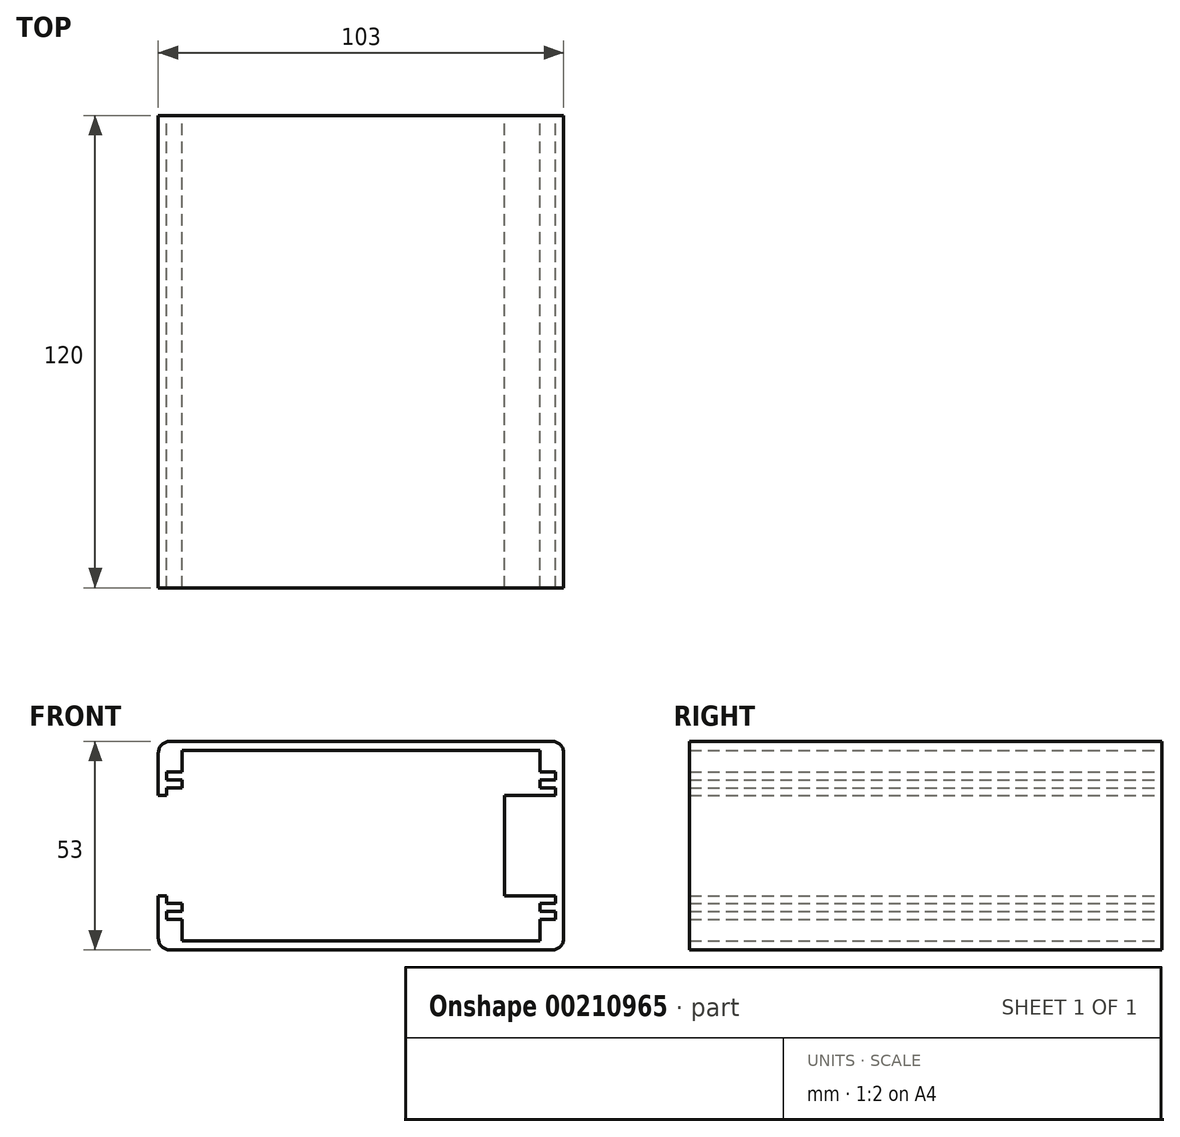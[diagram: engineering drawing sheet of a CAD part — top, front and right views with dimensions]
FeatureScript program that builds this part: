
annotation { "Feature Type Name" : "Feature", "Feature Type Description" : "" }
export const myFeature = defineFeature(function(context is Context, id is Id, definition is map)
    precondition{}
    {
        {
            var Q0;
            Q0=qCreatedBy(makeId("Front.planeOp"),FACE);
            var sketch = newSketch(context, id + "F0", { "sketchPlane" : qUnion([Q0])});
            skLineSegment(sketch, "E0.bottom", {"start": v(48.5, -26.5) * mm, "end": v(-48.5, -26.5) * mm});
            skLineSegment(sketch, "E0.top", {"start": v(48.5, 26.5) * mm, "end": v(-48.5, 26.5) * mm});
            skLineSegment(sketch, "E0.left", {"start": v(51.5, -23.5) * mm, "end": v(51.5, 23.5) * mm});
            skLineSegment(sketch, "E0.right", {"start": v(-51.5, -23.5) * mm, "end": v(-51.5, 23.5) * mm});
            skPoint(sketch, "E0.middle", {"position": v(0, 0) * mm});
            skPoint(sketch, "E1.visualSharp", {"position": v(-51.5, 26.5) * mm});
            skArc(sketch, "E1.filletArc", {"start": v(-48.5, 26.5) * mm, "mid": v(-50.62, 25.62) * mm, "end": v(-51.5, 23.5) * mm});
            skPoint(sketch, "E2.visualSharp", {"position": v(51.5, 26.5) * mm});
            skArc(sketch, "E2.filletArc", {"start": v(51.5, 23.5) * mm, "mid": v(50.62, 25.62) * mm, "end": v(48.5, 26.5) * mm});
            skPoint(sketch, "E3.visualSharp", {"position": v(51.5, -26.5) * mm});
            skArc(sketch, "E3.filletArc", {"start": v(48.5, -26.5) * mm, "mid": v(50.62, -25.62) * mm, "end": v(51.5, -23.5) * mm});
            skPoint(sketch, "E4.visualSharp", {"position": v(-51.5, -26.5) * mm});
            skArc(sketch, "E4.filletArc", {"start": v(-51.5, -23.5) * mm, "mid": v(-50.62, -25.62) * mm, "end": v(-48.5, -26.5) * mm});
            skLineSegment(sketch, "E5.bottom", {"start": v(45.5, -24.2) * mm, "end": v(-45.5, -24.21) * mm});
            skLineSegment(sketch, "E5.top", {"start": v(45.5, 24.21) * mm, "end": v(-45.5, 24.2) * mm});
            skLineSegment(sketch, "E5.left", {"start": v(45.5, -24.2) * mm, "end": v(45.5, -18.72) * mm});
            skLineSegment(sketch, "E5.right", {"start": v(-45.5, -24.21) * mm, "end": v(-45.5, -18.72) * mm});
            skLineSegment(sketch, "E6.bottom", {"start": v(-51.5, -12.73) * mm, "end": v(-36.5, -12.73) * mm});
            skLineSegment(sketch, "E6.top", {"start": v(-51.5, 12.72) * mm, "end": v(-36.5, 12.72) * mm});
            skLineSegment(sketch, "E6.left", {"start": v(-51.5, -12.73) * mm, "end": v(-51.5, 12.72) * mm});
            skLineSegment(sketch, "E6.right", {"start": v(-36.5, -12.73) * mm, "end": v(-36.5, 12.72) * mm});
            skLineSegment(sketch, "E7.MirrorCS", {"start": v(51.5, -12.73) * mm, "end": v(36.5, -12.73) * mm});
            skLineSegment(sketch, "E8.MirrorCS", {"start": v(51.5, 12.72) * mm, "end": v(36.5, 12.72) * mm});
            skLineSegment(sketch, "E9.MirrorCS", {"start": v(36.5, -12.73) * mm, "end": v(36.5, 12.72) * mm});
            skLineSegment(sketch, "E10.trimOffspring", {"start": v(-45.5, 14.73) * mm, "end": v(-45.5, 16.73) * mm});
            skLineSegment(sketch, "E11.trimOffspring", {"start": v(45.5, 14.73) * mm, "end": v(45.5, 16.73) * mm});
            skLineSegment(sketch, "E12", {"start": v(45.5, -14.73) * mm, "end": v(49.36, -14.73) * mm});
            skLineSegment(sketch, "E13", {"start": v(49.36, -14.73) * mm, "end": v(49.36, -12.73) * mm});
            skLineSegment(sketch, "E14", {"start": v(45.5, -16.73) * mm, "end": v(49.36, -16.73) * mm});
            skLineSegment(sketch, "E15", {"start": v(49.36, -16.73) * mm, "end": v(49.36, -18.72) * mm});
            skLineSegment(sketch, "E16", {"start": v(49.36, -18.72) * mm, "end": v(45.5, -18.72) * mm});
            skLineSegment(sketch, "E17.trimOffspring", {"start": v(45.5, -16.73) * mm, "end": v(45.5, -14.73) * mm});
            skLineSegment(sketch, "E18.MirrorCS", {"start": v(-49.36, -18.72) * mm, "end": v(-45.5, -18.72) * mm});
            skLineSegment(sketch, "E19.MirrorCS", {"start": v(-49.36, -16.73) * mm, "end": v(-49.36, -18.72) * mm});
            skLineSegment(sketch, "E20.MirrorCS", {"start": v(-45.5, -16.73) * mm, "end": v(-49.36, -16.73) * mm});
            skLineSegment(sketch, "E21.MirrorCS", {"start": v(-49.36, -14.73) * mm, "end": v(-49.36, -12.73) * mm});
            skLineSegment(sketch, "E22.MirrorCS", {"start": v(-45.5, -14.73) * mm, "end": v(-49.36, -14.73) * mm});
            skLineSegment(sketch, "E23.trimOffspring", {"start": v(-45.5, -16.73) * mm, "end": v(-45.5, -14.73) * mm});
            skLineSegment(sketch, "E24.MirrorCS", {"start": v(49.36, 18.72) * mm, "end": v(45.5, 18.72) * mm});
            skLineSegment(sketch, "E25.MirrorCS", {"start": v(49.36, 16.73) * mm, "end": v(49.36, 18.72) * mm});
            skLineSegment(sketch, "E26.MirrorCS", {"start": v(45.5, 16.73) * mm, "end": v(49.36, 16.73) * mm});
            skLineSegment(sketch, "E27.MirrorCS", {"start": v(45.5, 14.73) * mm, "end": v(49.36, 14.73) * mm});
            skLineSegment(sketch, "E28.MirrorCS", {"start": v(49.36, 14.73) * mm, "end": v(49.36, 12.73) * mm});
            skLineSegment(sketch, "E29.MirrorCS", {"start": v(-49.36, 18.72) * mm, "end": v(-45.5, 18.72) * mm});
            skLineSegment(sketch, "E30.MirrorCS", {"start": v(-49.36, 16.73) * mm, "end": v(-49.36, 18.72) * mm});
            skLineSegment(sketch, "E31.MirrorCS", {"start": v(-45.5, 16.73) * mm, "end": v(-49.36, 16.73) * mm});
            skLineSegment(sketch, "E32.MirrorCS", {"start": v(-49.36, 14.73) * mm, "end": v(-49.36, 12.73) * mm});
            skLineSegment(sketch, "E33.MirrorCS", {"start": v(-45.5, 14.73) * mm, "end": v(-49.36, 14.73) * mm});
            skLineSegment(sketch, "E34.trimOffspring", {"start": v(45.5, 18.72) * mm, "end": v(45.5, 24.21) * mm});
            skLineSegment(sketch, "E35.trimOffspring", {"start": v(-45.5, 18.72) * mm, "end": v(-45.5, 24.2) * mm});
            skSolve(sketch);
        }
        {
            var Q0;
            Q0=makeQuery(id+"F0.imprint","IMPRINT",FACE,{"disambiguationData":[TD([[makeQuery(id+"F0.imprint","IMPRINT",EDGE,{"derivedFrom":sQuery(id+"F0.wireOp",EDGE,"E0.top")}),1.0]])]});
            var Q1;
            {var subQ3=sQuery(id+"F0.wireOp",EDGE,"E6.left");Q1=makeQuery(id+"F0.imprint","IMPRINT",FACE,{"disambiguationData":[TD([[makeQuery(id+"F0.imprint","IMPRINT",EDGE,{"derivedFrom":subQ3}),-1.0]])]});}
            var Q2;
            Q2=makeQuery(id+"F0.imprint","IMPRINT",FACE,{"disambiguationData":[TD([[makeQuery(id+"F0.imprint","IMPRINT",EDGE,{"derivedFrom":sQuery(id+"F0.wireOp",EDGE,"E0.bottom")}),-1.0]])]});
            var Q3;
            {var subQ2=sQuery(id+"F0.wireOp",EDGE,"E9.MirrorCS");Q3=makeQuery(id+"F0.imprint","IMPRINT",FACE,{"disambiguationData":[TD([[makeQuery(id+"F0.imprint","IMPRINT",EDGE,{"derivedFrom":subQ2}),-1.0]])]});}
            extrude(context, id + "F1", {"entities" : qUnion([Q0, Q1, Q2, Q3]), "endBound" : BoundingType.SYMMETRIC, "depth" : 120 * mm});
        }
    });
